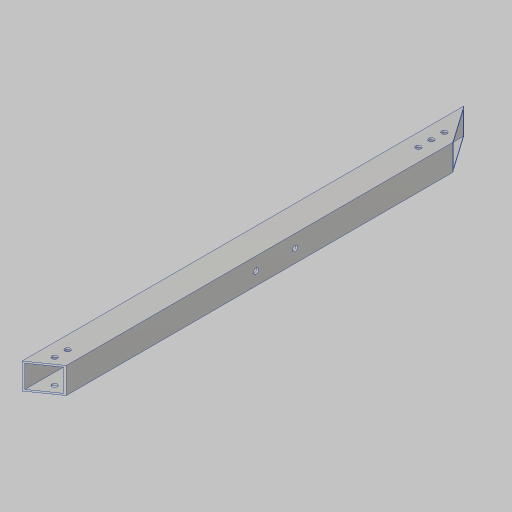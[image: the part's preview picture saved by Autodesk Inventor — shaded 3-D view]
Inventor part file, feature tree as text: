
AUTODESK INVENTOR PART (.ipt)
format: ipt  version: 2023.5 (Build 275446000, 446)  size: 223,744 bytes
history: native  units: in
note: dims shown in document units (in); Inventor stores cm internally (conversion verified against a paired STEP export)
features: sketch x3, extrude x2, hole x2, projected_geometry x2
ambient origin geometry x8: Origin, YZ Plane, XZ Plane, XY Plane, X Axis, Y Axis, Z Axis, Center Point
bodies: Solid1 (feature_tree)
feature tree (9):
  extrude  "Extrusion1"  TaperAngle=0.0deg  [1 undecoded]
  extrude  "Extrusion3"  Depth=0.75in
  hole  "Hole1"  [1 undecoded]
  hole  "Hole2"  [1 undecoded]
  sketch  "Sketch3"  dims[d4=0.0in d10=0.0in d11=0.0in]
  projected_geometry  "Projected Loop1"
  sketch  "Sketch4"  dims[d12=0.3779in d13=0.75in]
  sketch  "Sketch5"  dims[d14=1.5748in d16=0.5in d17=0.3937in d19=1.0in d21=0.201in d22=0.38in d23=0.385in d24=0.25in d25=0.5635in d26=1.0in d27=0.8108in d28=1.25in d29=1.1811in d31=0.5in d32=0.3937in d34=1.0in d36=1.5in d37=7.5in d38=0.201in d39=0.38in d40=0.385in d41=0.25in d42=0.5635in d43=1.0in d44=0.8108in]
  projected_geometry  "Project Cut Edges1"
note: 3 required parameter values undecoded (feature->parameter linkage not recoverable at this tier; creation-order binding heuristic only, values carry confidence <= 0.55)
